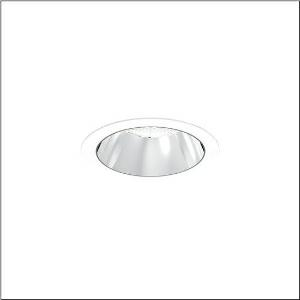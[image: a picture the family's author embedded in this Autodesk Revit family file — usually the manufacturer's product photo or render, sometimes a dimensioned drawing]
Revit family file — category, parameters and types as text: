
# Revit family: lunis_21_l_51db15ed91c
name_source: partatom
category: Lighting Fixtures
units: mm (PartAtom-declared; Revit-internal decimal feet)

## family parameters
Cut with Voids When Loaded = No
Host = Face
Light Source = No
Part Type = Normal
Room Calculation Point = No
Round Connector Dimension = Use Diameter
Shared = No

## types (1)
- --- (1 x LED, 4060 lm, 25.4 W, 6500K)
    Apparent Load = 25 VA
    CIE Flux Codes = 93 100 100 100 100
    Color Rendering = 80
    Color Temperature = 6500K
    Default Elevation = 1800 mm
    Description = Lunis 21,  L, downlight, light control with lens, of PMMA, anti glare with reflector, of PC, highly specular, light emission: direct distribution, LED rated luminous flux: 2.120lm, light colour: 830/840/865, with terminal, 5-pole, mains connection: 220..240V, AC/DC, 0/50..60Hz, housing, round, of diecast aluminium, traffic white (RAL 9016), diameter: 165mm, clamping range: 1..40mm, protection rating (complete): IP20, protection rating (on room side): IP54, insulation class (complete): insulation class II (safety insulation), certification: CE, impact resistance: IK03, packaging unit: 1 piece
    Height = 0 mm  [stored 0 ft]
    Lamp = 1 x LED
    Lamp Light Flux = 4060 lm
    Lamp Power = 25.4 W
    Lamp count = 1
    Length = 165 mm
    Luminous efficacy = 160 lm/W
    Manufacturer = Siteco
    ModVariant = No
    Model = 51DB15ED91C
    Mounting Place = Ceiling
    Mounting Type = Recessed
    Number of Poles = 1
    OnlyDefault = Yes
    Power Factor = 1
    Product Name = Lunis 21 L
    Product group = downlight
    ProductGroupID = 401
    Protection Class = Protection class II
    Protection Degree = IP 20
    RLX_Detail_Level = 1
    RLX_Emergency_Light_Flux = 0 lm
    RLX_Emergency_Type = 0
    RLX_Emergency_Type_DB = No
    RlxData = <blob elided: 18237 chars, md5=af39c86c>
    Socket = socket
    Standby Power = 0 W
    System Light Flux = 4060 lm
    System Power = 25 W
    Type Comments = individual setting: colour temperature 6500K, luminous flux: 100 % | (ON | ON | OFF | OFF) | 700 mA
    Type Image = l_1291167.jpg
    URL = http://relux.com
    VarID = @adj_040417
    Voltage = 0 V
    Weight = 0.00 kg
    Width = 0 mm  [stored 0 ft]

note: [stored X ft] marks values corroborated as IEEE doubles in the binary element streams (Revit-internal decimal feet)

## geometry (parser evidence)
native form markers: Blend x4, Sweep x10
no freeform markers — native parametric forms only
